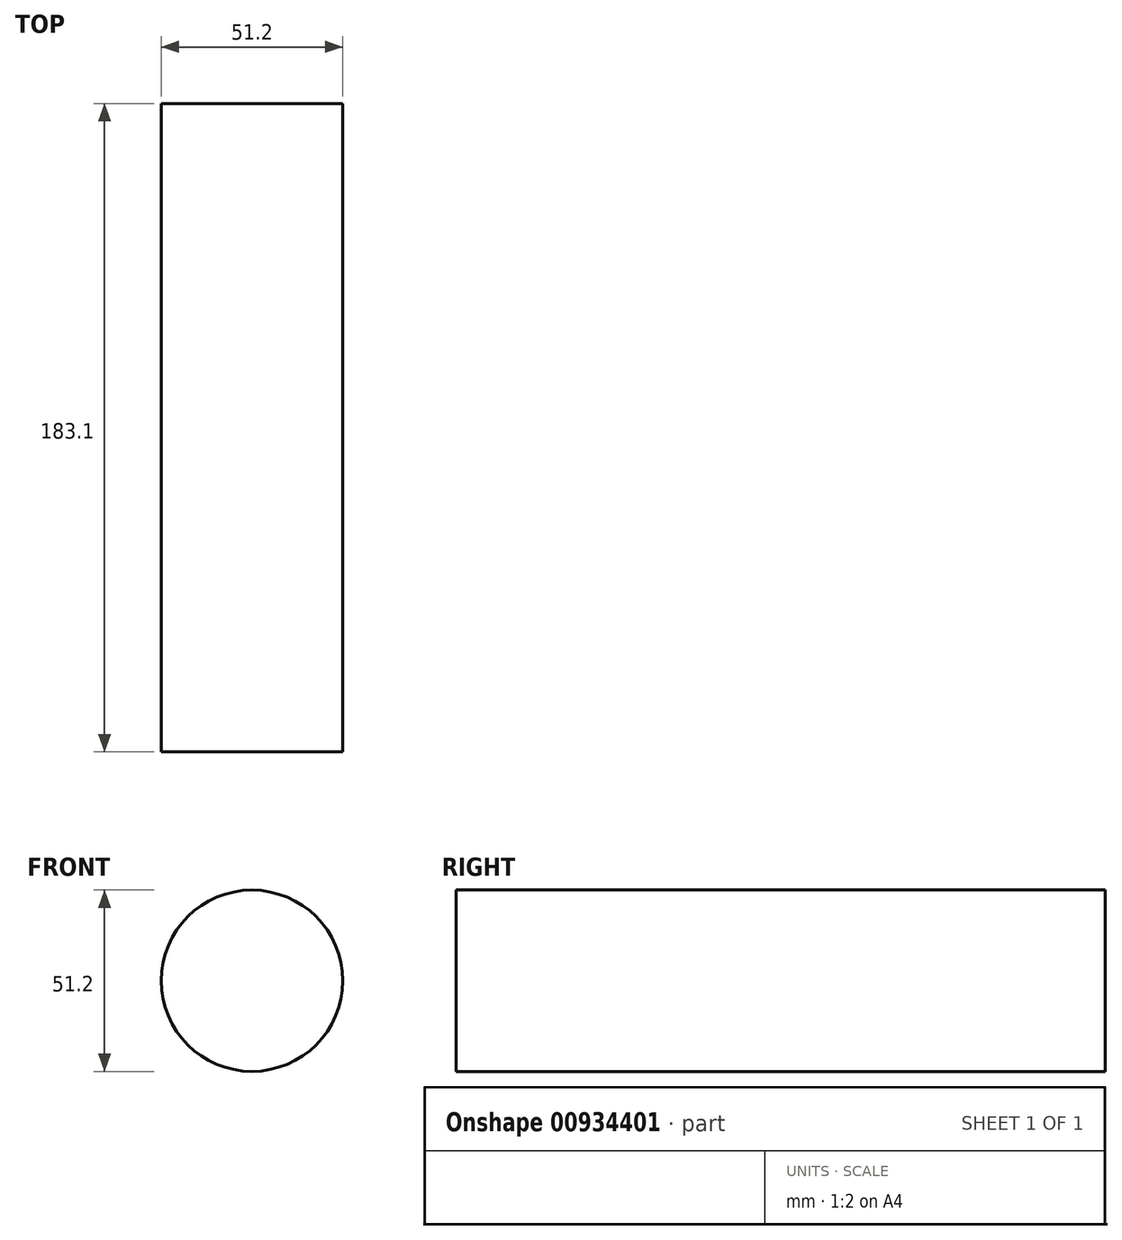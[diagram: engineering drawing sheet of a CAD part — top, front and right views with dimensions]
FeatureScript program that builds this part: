
annotation { "Feature Type Name" : "Feature", "Feature Type Description" : "" }
export const myFeature = defineFeature(function(context is Context, id is Id, definition is map)
    precondition{}
    {
        {
            var Q0;
            Q0=qCreatedBy(makeId("Front.planeOp"),FACE);
            var sketch = newSketch(context, id + "F0", { "sketchPlane" : qUnion([Q0])});
            skCircle(sketch, "E0", {"center": v(0, 0) * mm, "radius": 25.6 * mm});
            skSolve(sketch);
        }
        {
            var Q0;
            Q0 = qSketchRegion(id + "F0", true);
            var Q1;
            Q1=makeQuery(id+"F0.imprint","IMPRINT",FACE,{"disambiguationData":[TD([[makeQuery(id+"F0.imprint","IMPRINT",EDGE,{"derivedFrom":sQuery(id+"F0.wireOp",EDGE,"E0")}),1.0]])]});
            extrude(context, id + "F1", {"entities" : qUnion([Q0, Q1]), "depth" : 183.1 * mm, "offsetDistance" : 25.4 * mm});
        }
    });
